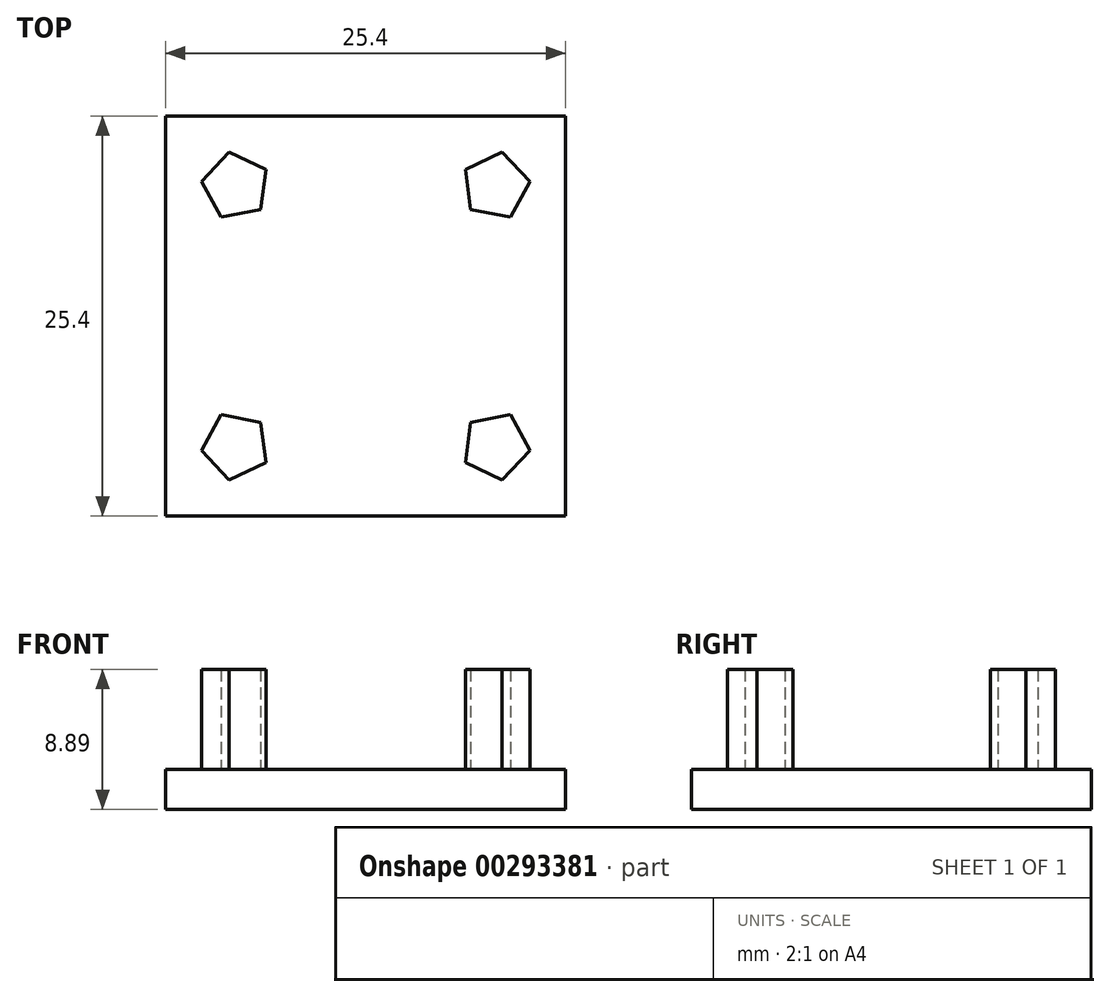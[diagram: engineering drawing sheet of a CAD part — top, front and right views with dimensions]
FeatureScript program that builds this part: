
annotation { "Feature Type Name" : "Feature", "Feature Type Description" : "" }
export const myFeature = defineFeature(function(context is Context, id is Id, definition is map)
    precondition{}
    {
        {
            var Q0;
            Q0=qCreatedBy(makeId("Top.planeOp"),FACE);
            var sketch = newSketch(context, id + "F0", { "sketchPlane" : qUnion([Q0])});
            skLineSegment(sketch, "E0.bottom", {"start": v(1.67, -7.69) * mm, "end": v(27.07, -7.69) * mm});
            skLineSegment(sketch, "E0.top", {"start": v(1.67, -33.09) * mm, "end": v(27.07, -33.09) * mm});
            skLineSegment(sketch, "E0.left", {"start": v(1.67, -7.69) * mm, "end": v(1.67, -33.09) * mm});
            skLineSegment(sketch, "E0.right", {"start": v(27.07, -7.69) * mm, "end": v(27.07, -33.09) * mm});
            skLineSegment(sketch, "E1.0", {"start": v(8.04, -11.08) * mm, "end": v(7.71, -13.63) * mm});
            skLineSegment(sketch, "E1.1", {"start": v(7.71, -13.63) * mm, "end": v(5.18, -14.11) * mm});
            skLineSegment(sketch, "E1.2", {"start": v(5.18, -14.11) * mm, "end": v(3.94, -11.85) * mm});
            skLineSegment(sketch, "E1.3", {"start": v(3.94, -11.85) * mm, "end": v(5.7, -9.98) * mm});
            skLineSegment(sketch, "E1.4", {"start": v(5.7, -9.98) * mm, "end": v(8.04, -11.08) * mm});
            skLineSegment(sketch, "E2.MirrorCS", {"start": v(23.03, -9.98) * mm, "end": v(20.7, -11.08) * mm});
            skLineSegment(sketch, "E3.MirrorCS", {"start": v(23.56, -14.11) * mm, "end": v(24.8, -11.85) * mm});
            skLineSegment(sketch, "E4.MirrorCS", {"start": v(21.03, -13.63) * mm, "end": v(23.56, -14.11) * mm});
            skLineSegment(sketch, "E5.MirrorCS", {"start": v(20.7, -11.08) * mm, "end": v(21.03, -13.63) * mm});
            skLineSegment(sketch, "E6.MirrorCS", {"start": v(24.8, -11.85) * mm, "end": v(23.03, -9.98) * mm});
            skLineSegment(sketch, "E7.MirrorCS", {"start": v(23.56, -26.66) * mm, "end": v(24.8, -28.92) * mm});
            skLineSegment(sketch, "E8.MirrorCS", {"start": v(23.03, -30.8) * mm, "end": v(20.7, -29.7) * mm});
            skLineSegment(sketch, "E9.MirrorCS", {"start": v(20.7, -29.7) * mm, "end": v(21.03, -27.14) * mm});
            skLineSegment(sketch, "E10.MirrorCS", {"start": v(21.03, -27.14) * mm, "end": v(23.56, -26.66) * mm});
            skLineSegment(sketch, "E11.MirrorCS", {"start": v(24.8, -28.92) * mm, "end": v(23.03, -30.8) * mm});
            skLineSegment(sketch, "E12.MirrorCS", {"start": v(5.7, -30.8) * mm, "end": v(8.04, -29.7) * mm});
            skLineSegment(sketch, "E13.MirrorCS", {"start": v(5.18, -26.66) * mm, "end": v(3.94, -28.92) * mm});
            skLineSegment(sketch, "E14.MirrorCS", {"start": v(8.04, -29.7) * mm, "end": v(7.71, -27.14) * mm});
            skLineSegment(sketch, "E15.MirrorCS", {"start": v(7.71, -27.14) * mm, "end": v(5.18, -26.66) * mm});
            skLineSegment(sketch, "E16.MirrorCS", {"start": v(3.94, -28.92) * mm, "end": v(5.7, -30.8) * mm});
            skSolve(sketch);
        }
        {
            var Q0;
            Q0=makeQuery(id+"F0.imprint","IMPRINT",FACE,{"disambiguationData":[TD([[makeQuery(id+"F0.imprint","IMPRINT",EDGE,{"derivedFrom":sQuery(id+"F0.wireOp",EDGE,"E0.bottom")}),-1.0]])]});
            extrude(context, id + "F1", {"entities" : qUnion([Q0]), "depth" : 2.54 * mm});
        }
        {
            var Q0;
            Q0=makeQuery(id+"F0.imprint","IMPRINT",FACE,{"disambiguationData":[TD([[makeQuery(id+"F0.imprint","IMPRINT",EDGE,{"derivedFrom":sQuery(id+"F0.wireOp",EDGE,"E1.0")}),-1.0]])]});
            var Q1;
            Q1=makeQuery(id+"F0.imprint","IMPRINT",FACE,{"disambiguationData":[TD([[makeQuery(id+"F0.imprint","IMPRINT",EDGE,{"derivedFrom":sQuery(id+"F0.wireOp",EDGE,"E2.MirrorCS")}),1.0]])]});
            var Q2;
            Q2=makeQuery(id+"F0.imprint","IMPRINT",FACE,{"disambiguationData":[TD([[makeQuery(id+"F0.imprint","IMPRINT",EDGE,{"derivedFrom":sQuery(id+"F0.wireOp",EDGE,"E7.MirrorCS")}),-1.0]])]});
            var Q3;
            Q3=makeQuery(id+"F0.imprint","IMPRINT",FACE,{"disambiguationData":[TD([[makeQuery(id+"F0.imprint","IMPRINT",EDGE,{"derivedFrom":sQuery(id+"F0.wireOp",EDGE,"E12.MirrorCS")}),1.0]])]});
            extrude(context, id + "F2", {"entities" : qUnion([Q0, Q1, Q2, Q3]), "operationType" : NewBodyOperationType.ADD, "depth" : 8.9 * mm});
        }
    });
